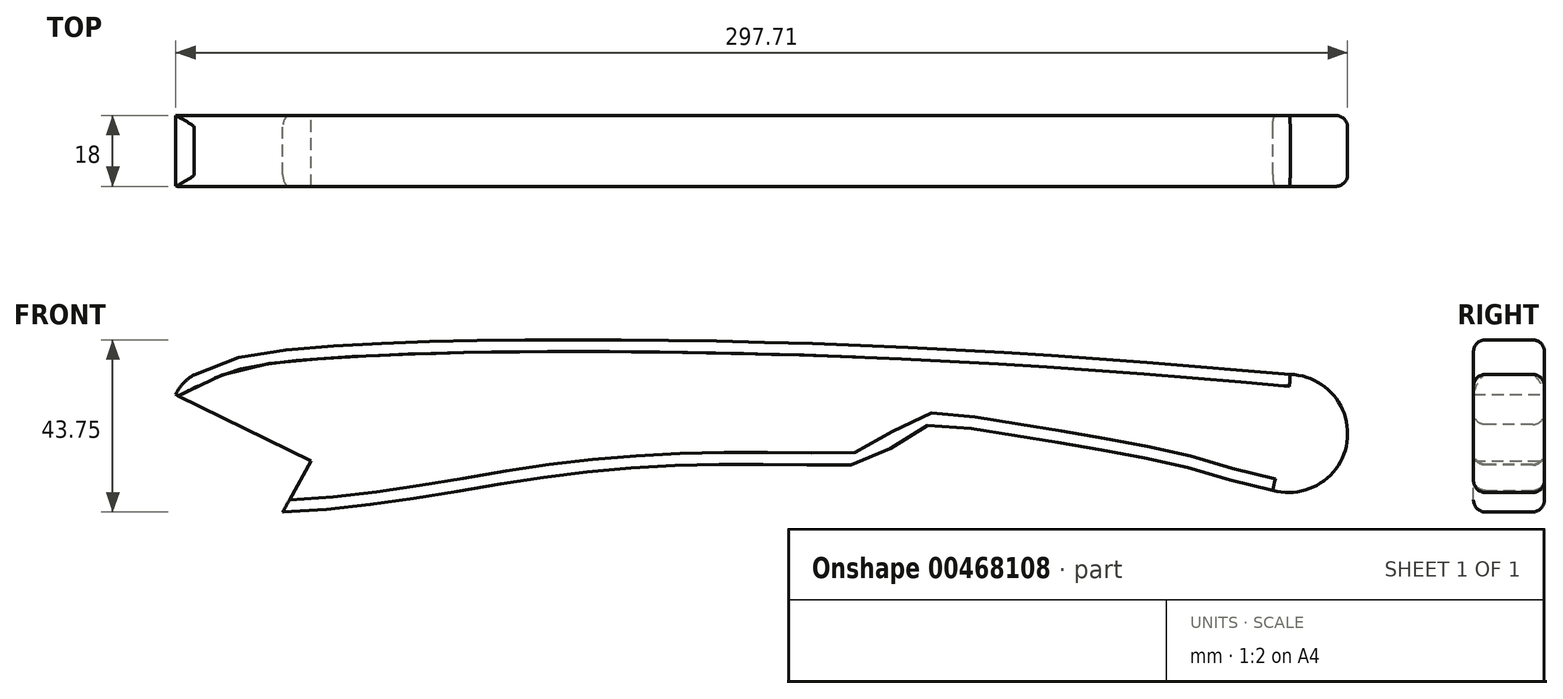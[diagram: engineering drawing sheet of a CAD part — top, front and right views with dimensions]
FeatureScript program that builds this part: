
annotation { "Feature Type Name" : "Feature", "Feature Type Description" : "" }
export const myFeature = defineFeature(function(context is Context, id is Id, definition is map)
    precondition{}
    {
        {
            var Q0;
            Q0=qCreatedBy(makeId("Front.planeOp"),FACE);
            var sketch = newSketch(context, id + "F0", { "sketchPlane" : qUnion([Q0])});
            skFitSpline(sketch, "E0", {"points": [v(-144.03, 0) * mm, v(-126.92, 5.56) * mm, v(0, 8.29) * mm, v(134.47, 0.08) * mm], "startDerivative": vector(100.37, 50.71) * mm, "endDerivative": vector(295.77, -25.93) * mm});
            skArc(sketch, "E1", {"start": v(130.04, -29.36) * mm, "mid": v(148.9, -17.14) * mm, "end": v(134.47, 0.08) * mm});
            skFitSpline(sketch, "E2", {"points": [v(130.04, -29.36) * mm, v(111.39, -24.32) * mm, v(82.66, -18.4) * mm, v(53.02, -13.56) * mm, v(39.97, -13.63) * mm, v(29.78, -21) * mm, v(17.65, -22.95) * mm, v(-41.82, -24.41) * mm, v(-121.47, -34.87) * mm], "startDerivative": vector(-228.58, 39.23) * mm, "endDerivative": vector(-397.62, -14.51) * mm});
            skLineSegment(sketch, "E3", {"start": v(-121.47, -34.87) * mm, "end": v(-114.32, -21.86) * mm});
            skLineSegment(sketch, "E4", {"start": v(-114.32, -21.86) * mm, "end": v(-148.64, -5.05) * mm});
            skFitSpline(sketch, "E5", {"points": [v(-148.64, -5.05) * mm, v(-144.03, 0) * mm], "startDerivative": vector(2.98, 8.03) * mm, "endDerivative": vector(2.98, 1.86) * mm});
            skSolve(sketch);
        }
        {
            var Q0;
            Q0 = qSketchRegion(id + "F0", true);
            extrude(context, id + "F1", {"entities" : qUnion([Q0]), "depth" : 18 * mm});
        }
        {
            var Q0;
            Q0=makeQuery(id+"F1.opExtrude","CAP_EDGE",EDGE,{"disambiguationData":[OSD([sQuery(id+"F0.wireOp",EDGE,"E0")])],"isStart":false});
            var Q1;
            Q1=makeQuery(id+"F1.opExtrude","CAP_EDGE",EDGE,{"disambiguationData":[OSD([sQuery(id+"F0.wireOp",EDGE,"E0")])],"isStart":true});
            var Q2;
            Q2=makeQuery(id+"F1.opExtrude","CAP_EDGE",EDGE,{"disambiguationData":[OSD([sQuery(id+"F0.wireOp",EDGE,"E1")])],"isStart":false});
            var Q3;
            Q3=makeQuery(id+"F1.opExtrude","CAP_EDGE",EDGE,{"disambiguationData":[OSD([sQuery(id+"F0.wireOp",EDGE,"E2")])],"isStart":false});
            var Q4;
            Q4=makeQuery(id+"F1.opExtrude","CAP_EDGE",EDGE,{"disambiguationData":[OSD([sQuery(id+"F0.wireOp",EDGE,"E1")])],"isStart":true});
            var Q5;
            Q5=makeQuery(id+"F1.opExtrude","CAP_EDGE",EDGE,{"disambiguationData":[OSD([sQuery(id+"F0.wireOp",EDGE,"E2")])],"isStart":true});
            fillet(context, id + "F2", {"entities" : qUnion([Q0, Q1, Q2, Q3, Q4, Q5]), "radius" : 3 * mm, "tangentPropagation" : true, "allowEdgeOverflow" : false});
        }
    });
